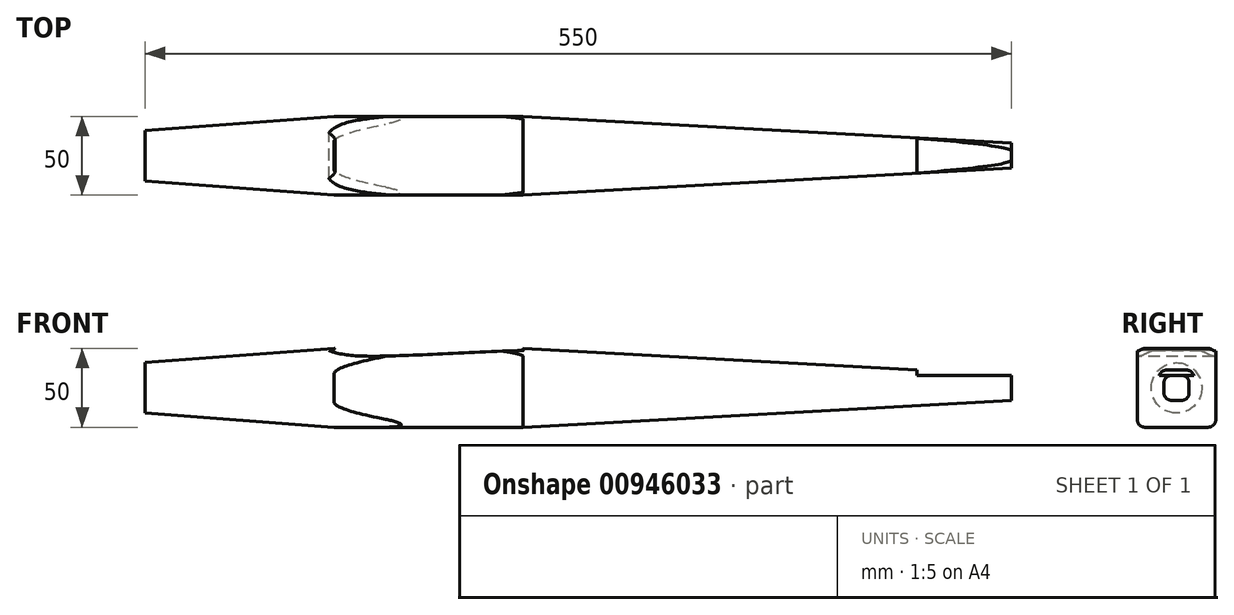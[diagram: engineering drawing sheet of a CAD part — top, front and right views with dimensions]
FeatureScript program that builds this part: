
annotation { "Feature Type Name" : "Feature", "Feature Type Description" : "" }
export const myFeature = defineFeature(function(context is Context, id is Id, definition is map)
    precondition{}
    {
        {
            var Q0;
            Q0=qCreatedBy(makeId("Front.planeOp"),FACE);
            var sketch = newSketch(context, id + "F0", { "sketchPlane" : qUnion([Q0])});
            skLineSegment(sketch, "E0.bottom", {"start": v(275, -25) * mm, "end": v(-155, -25) * mm});
            skLineSegment(sketch, "E0.top", {"start": v(275, 25) * mm, "end": v(-35, 25) * mm});
            skLineSegment(sketch, "E0.left", {"start": v(275, -25) * mm, "end": v(275, 25) * mm});
            skLineSegment(sketch, "E0.right", {"start": v(-275, -16) * mm, "end": v(-275, 16) * mm});
            skPoint(sketch, "E0.middle", {"position": v(0, 0) * mm});
            skPoint(sketch, "E1", {"position": v(-155, 25) * mm});
            skPoint(sketch, "E2", {"position": v(-155, -25) * mm});
            skPoint(sketch, "E3", {"position": v(-35, 25) * mm});
            skPoint(sketch, "E4", {"position": v(-35, -25) * mm});
            skPoint(sketch, "E5", {"position": v(275, 0) * mm});
            skLineSegment(sketch, "E6", {"start": v(-35, 25) * mm, "end": v(215, 11.3) * mm});
            skLineSegment(sketch, "E7", {"start": v(-35, -25) * mm, "end": v(275, -8.01) * mm});
            skPoint(sketch, "E8", {"position": v(-275, 0) * mm});
            skPoint(sketch, "E9", {"position": v(-275, 16) * mm});
            skPoint(sketch, "E10", {"position": v(-275, -16) * mm});
            skLineSegment(sketch, "E11", {"start": v(-155, 25) * mm, "end": v(-275, 16) * mm});
            skLineSegment(sketch, "E12", {"start": v(-155, -25) * mm, "end": v(-275, -16) * mm});
            skPoint(sketch, "E13.orphan", {"position": v(-275, 25) * mm});
            skPoint(sketch, "E14.orphan", {"position": v(-275, -25) * mm});
            skLineSegment(sketch, "E15.left", {"start": v(-34.96, 23.58) * mm, "end": v(-34.96, 23.7) * mm});
            skPoint(sketch, "E15.middle", {"position": v(-94.96, 23.7) * mm});
            skPoint(sketch, "E16", {"position": v(-114.96, 27.7) * mm});
            skPoint(sketch, "E17", {"position": v(-114.96, 19.7) * mm});
            skPoint(sketch, "E18", {"position": v(-158.36, 23.7) * mm});
            skPoint(sketch, "E19", {"position": v(-133.23, 27.3) * mm});
            skPoint(sketch, "E20", {"position": v(-133.23, 20.1) * mm});
            skFitSpline(sketch, "E21", {"points": [v(-158.36, 23.7) * mm, v(-133.23, 27.3) * mm, v(-34.96, 23.7) * mm], "startDerivative": vector(57.85, 22.18) * mm, "endDerivative": vector(172.34, -4.26) * mm});
            skFitSpline(sketch, "E22", {"points": [v(-158.36, 23.7) * mm, v(-133.23, 20.1) * mm, v(-34.96, 23.7) * mm], "startDerivative": vector(57.86, -22.18) * mm, "endDerivative": vector(172.34, 4.26) * mm});
            skArc(sketch, "E23", {"start": v(-153.84, 25.15) * mm, "mid": v(-154.96, 23.7) * mm, "end": v(-153.84, 22.25) * mm});
            skPoint(sketch, "E23.centerSnap0", {"position": v(-154.96, 23.7) * mm});
            skPoint(sketch, "E24.orphan", {"position": v(-154.96, 27.7) * mm});
            skPoint(sketch, "E25.orphan", {"position": v(-154.96, 19.7) * mm});
            skPoint(sketch, "E26.orphan", {"position": v(-34.96, 27.7) * mm});
            skLineSegment(sketch, "E27", {"start": v(-34.96, 23.58) * mm, "end": v(-34.96, 23.97) * mm});
            skPoint(sketch, "E28", {"position": v(-34.96, 23.72) * mm});
            skPoint(sketch, "E29", {"position": v(-34.96, 23.68) * mm});
            skPoint(sketch, "E30.orphan", {"position": v(-34.96, 19.7) * mm});
            skLineSegment(sketch, "E31", {"start": v(-35, 25) * mm, "end": v(-34.96, 23.97) * mm});
            skLineSegment(sketch, "E32.trimOffspring", {"start": v(-69.96, 25) * mm, "end": v(-155, 25) * mm});
            skLineSegment(sketch, "E33", {"start": v(275, 8) * mm, "end": v(215, 8) * mm});
            skLineSegment(sketch, "E34", {"start": v(215, 8) * mm, "end": v(215, 11.3) * mm});
            skSolve(sketch);
        }
        {
            var Q0;
            Q0=qCreatedBy(makeId("Top.planeOp"),FACE);
            var sketch = newSketch(context, id + "F1", { "sketchPlane" : qUnion([Q0])});
            skLineSegment(sketch, "E35.bottom", {"start": v(275, -25) * mm, "end": v(-275, -25) * mm});
            skLineSegment(sketch, "E35.top", {"start": v(275, 25) * mm, "end": v(-275, 25) * mm});
            skLineSegment(sketch, "E35.left", {"start": v(275, -25) * mm, "end": v(275, 25) * mm});
            skLineSegment(sketch, "E35.right", {"start": v(-275, -25) * mm, "end": v(-275, 25) * mm});
            skPoint(sketch, "E35.middle", {"position": v(0, 0) * mm});
            skPoint(sketch, "E36", {"position": v(-155, 25) * mm});
            skPoint(sketch, "E37", {"position": v(-35, 25) * mm});
            skLineSegment(sketch, "E38", {"start": v(-35, 25) * mm, "end": v(275, 8) * mm});
            skPoint(sketch, "E39", {"position": v(-35, -25) * mm});
            skLineSegment(sketch, "E40", {"start": v(-35, -25) * mm, "end": v(275, -8) * mm});
            skPoint(sketch, "E41", {"position": v(-155, -25) * mm});
            skPoint(sketch, "E42", {"position": v(-275, 0) * mm});
            skPoint(sketch, "E43", {"position": v(-275, 16) * mm});
            skPoint(sketch, "E44", {"position": v(-275, -16) * mm});
            skLineSegment(sketch, "E45", {"start": v(-155, 25) * mm, "end": v(-275, 16) * mm});
            skLineSegment(sketch, "E46", {"start": v(-155, -25) * mm, "end": v(-275, -16) * mm});
            skSolve(sketch);
        }
        {
            var Q0;
            {var subQ0=sQuery(id+"F0.wireOp",EDGE,"E0.right");Q0=makeQuery(id+"F0.imprint","IMPRINT",FACE,{"disambiguationData":[TD([[makeQuery(id+"F0.imprint","IMPRINT",EDGE,{"derivedFrom":subQ0}),-1.0]])]});}
            extrude(context, id + "F2", {"entities" : qUnion([Q0]), "endBound" : BoundingType.SYMMETRIC, "depth" : 50 * mm, "offsetDistance" : 25 * mm});
        }
        {
            var Q0;
            {var subQ3=sQuery(id+"F1.wireOp",EDGE,"E38");Q0=makeQuery(id+"F1.imprint","IMPRINT",FACE,{"disambiguationData":[TD([[makeQuery(id+"F1.imprint","IMPRINT",EDGE,{"derivedFrom":subQ3}),1.0]])]});}
            var Q1;
            {var subQ3=sQuery(id+"F1.wireOp",EDGE,"E40");Q1=makeQuery(id+"F1.imprint","IMPRINT",FACE,{"disambiguationData":[TD([[makeQuery(id+"F1.imprint","IMPRINT",EDGE,{"derivedFrom":subQ3}),-1.0]])]});}
            extrude(context, id + "F3", {"entities" : qUnion([Q0, Q1]), "operationType" : NewBodyOperationType.REMOVE, "endBound" : BoundingType.SYMMETRIC, "oppositeDirection" : true, "depth" : 50 * mm, "offsetDistance" : 25 * mm});
        }
        {
            var Q0;
            {var subQ3=sQuery(id+"F1.wireOp",EDGE,"E45");Q0=makeQuery(id+"F1.imprint","IMPRINT",FACE,{"disambiguationData":[TD([[makeQuery(id+"F1.imprint","IMPRINT",EDGE,{"derivedFrom":subQ3}),-1.0]])]});}
            var Q1;
            {var subQ3=sQuery(id+"F1.wireOp",EDGE,"E46");Q1=makeQuery(id+"F1.imprint","IMPRINT",FACE,{"disambiguationData":[TD([[makeQuery(id+"F1.imprint","IMPRINT",EDGE,{"derivedFrom":subQ3}),1.0]])]});}
            var Q2;
            {var subQ3=sQuery(id+"F1.wireOp",EDGE,"E40");Q2=makeQuery(id+"F1.imprint","IMPRINT",FACE,{"disambiguationData":[TD([[makeQuery(id+"F1.imprint","IMPRINT",EDGE,{"derivedFrom":subQ3}),-1.0]])]});}
            var Q3;
            {var subQ3=sQuery(id+"F1.wireOp",EDGE,"E38");Q3=makeQuery(id+"F1.imprint","IMPRINT",FACE,{"disambiguationData":[TD([[makeQuery(id+"F1.imprint","IMPRINT",EDGE,{"derivedFrom":subQ3}),1.0]])]});}
            extrude(context, id + "F4", {"entities" : qUnion([Q0, Q1, Q2, Q3]), "operationType" : NewBodyOperationType.REMOVE, "endBound" : BoundingType.SYMMETRIC, "oppositeDirection" : true, "depth" : 50 * mm, "offsetDistance" : 25 * mm});
        }
        {
            var Q0;
            Q0=makeQuery(id+"F2.opExtrude","SWEPT_FACE",FACE,{"disambiguationData":[OSD([sQuery(id+"F0.wireOp",EDGE,"E0.right")])]});
            var sketch = newSketch(context, id + "F5", { "sketchPlane" : qUnion([Q0])});
            skCircle(sketch, "E47", {"center": v(0, 0) * mm, "radius": 16 * mm});
            skSolve(sketch);
        }
        {
            var Q0;
            Q0=makeQuery(id+"F4.boolean.opBoolean","INTERSECT",EDGE,{"derivedFrom":[makeQuery(id+"F2.opExtrude","SWEPT_FACE",FACE,{"disambiguationData":[OSD([sQuery(id+"F0.wireOp",EDGE,"E11")])]}),makeQuery(id+"F4.opExtrude","SWEPT_FACE",FACE,{"disambiguationData":[OSD([sQuery(id+"F1.wireOp",EDGE,"E46")])]})]});
            var Q1;
            Q1=makeQuery(id+"F4.boolean.opBoolean","INTERSECT",EDGE,{"derivedFrom":[makeQuery(id+"F2.opExtrude","SWEPT_FACE",FACE,{"disambiguationData":[OSD([sQuery(id+"F0.wireOp",EDGE,"E11")])]}),makeQuery(id+"F4.opExtrude","SWEPT_FACE",FACE,{"disambiguationData":[OSD([sQuery(id+"F1.wireOp",EDGE,"E45")])]})]});
            var Q2;
            Q2=makeQuery(id+"F4.boolean.opBoolean","INTERSECT",EDGE,{"derivedFrom":[makeQuery(id+"F2.opExtrude","SWEPT_FACE",FACE,{"disambiguationData":[OSD([sQuery(id+"F0.wireOp",EDGE,"E12")])]}),makeQuery(id+"F4.opExtrude","SWEPT_FACE",FACE,{"disambiguationData":[OSD([sQuery(id+"F1.wireOp",EDGE,"E45")])]})]});
            var Q3;
            Q3=makeQuery(id+"F4.boolean.opBoolean","INTERSECT",EDGE,{"derivedFrom":[makeQuery(id+"F2.opExtrude","SWEPT_FACE",FACE,{"disambiguationData":[OSD([sQuery(id+"F0.wireOp",EDGE,"E12")])]}),makeQuery(id+"F4.opExtrude","SWEPT_FACE",FACE,{"disambiguationData":[OSD([sQuery(id+"F1.wireOp",EDGE,"E46")])]})]});
            fillet(context, id + "F6", {"entities" : qUnion([Q0, Q1, Q2, Q3]), "radius" : 16 * mm, "tangentPropagation" : true, "allowEdgeOverflow" : false});
        }
        {
            var Q0;
            Q0=makeQuery(id+"F2.opExtrude","CAP_EDGE",EDGE,{"disambiguationData":[OSD([sQuery(id+"F0.wireOp",EDGE,"E0.bottom")])],"isStart":false});
            fillet(context, id + "F7", {"entities" : qUnion([Q0]), "radius" : 5 * mm, "tangentPropagation" : true, "allowEdgeOverflow" : false});
        }
        {
            var Q0;
            Q0=makeQuery(id+"F3.boolean.opBoolean","INTERSECT",EDGE,{"derivedFrom":[makeQuery(id+"F2.opExtrude","SWEPT_FACE",FACE,{"disambiguationData":[OSD([sQuery(id+"F0.wireOp",EDGE,"E6")])]}),makeQuery(id+"F3.opExtrude","SWEPT_FACE",FACE,{"disambiguationData":[OSD([sQuery(id+"F1.wireOp",EDGE,"E40")])]})]});
            var Q1;
            Q1=makeQuery(id+"F3.boolean.opBoolean","INTERSECT",EDGE,{"derivedFrom":[makeQuery(id+"F2.opExtrude","SWEPT_FACE",FACE,{"disambiguationData":[OSD([sQuery(id+"F0.wireOp",EDGE,"E7")])]}),makeQuery(id+"F3.opExtrude","SWEPT_FACE",FACE,{"disambiguationData":[OSD([sQuery(id+"F1.wireOp",EDGE,"E40")])]})]});
            fillet(context, id + "F8", {"entities" : qUnion([Q0, Q1]), "radius" : 5 * mm, "tangentPropagation" : true, "allowEdgeOverflow" : false});
        }
        {
            var Q0;
            Q0=makeQuery(id+"F3.boolean.opBoolean","INTERSECT",EDGE,{"derivedFrom":[makeQuery(id+"F2.opExtrude","SWEPT_FACE",FACE,{"disambiguationData":[OSD([sQuery(id+"F0.wireOp",EDGE,"E6")])]}),makeQuery(id+"F3.opExtrude","SWEPT_FACE",FACE,{"disambiguationData":[OSD([sQuery(id+"F1.wireOp",EDGE,"E38")])]})]});
            var Q1;
            Q1=makeQuery(id+"F3.boolean.opBoolean","INTERSECT",EDGE,{"derivedFrom":[makeQuery(id+"F2.opExtrude","SWEPT_FACE",FACE,{"disambiguationData":[OSD([sQuery(id+"F0.wireOp",EDGE,"E7")])]}),makeQuery(id+"F3.opExtrude","SWEPT_FACE",FACE,{"disambiguationData":[OSD([sQuery(id+"F1.wireOp",EDGE,"E38")])]})]});
            fillet(context, id + "F9", {"entities" : qUnion([Q0, Q1]), "radius" : 5 * mm, "tangentPropagation" : true, "allowEdgeOverflow" : false});
        }
        {
            var Q0;
            Q0=makeQuery(id+"F2.opExtrude","CAP_EDGE",EDGE,{"disambiguationData":[OSD([sQuery(id+"F0.wireOp",EDGE,"E0.bottom")])],"isStart":true});
            fillet(context, id + "F10", {"entities" : qUnion([Q0]), "radius" : 5 * mm, "tangentPropagation" : true, "allowEdgeOverflow" : false});
        }
    });
